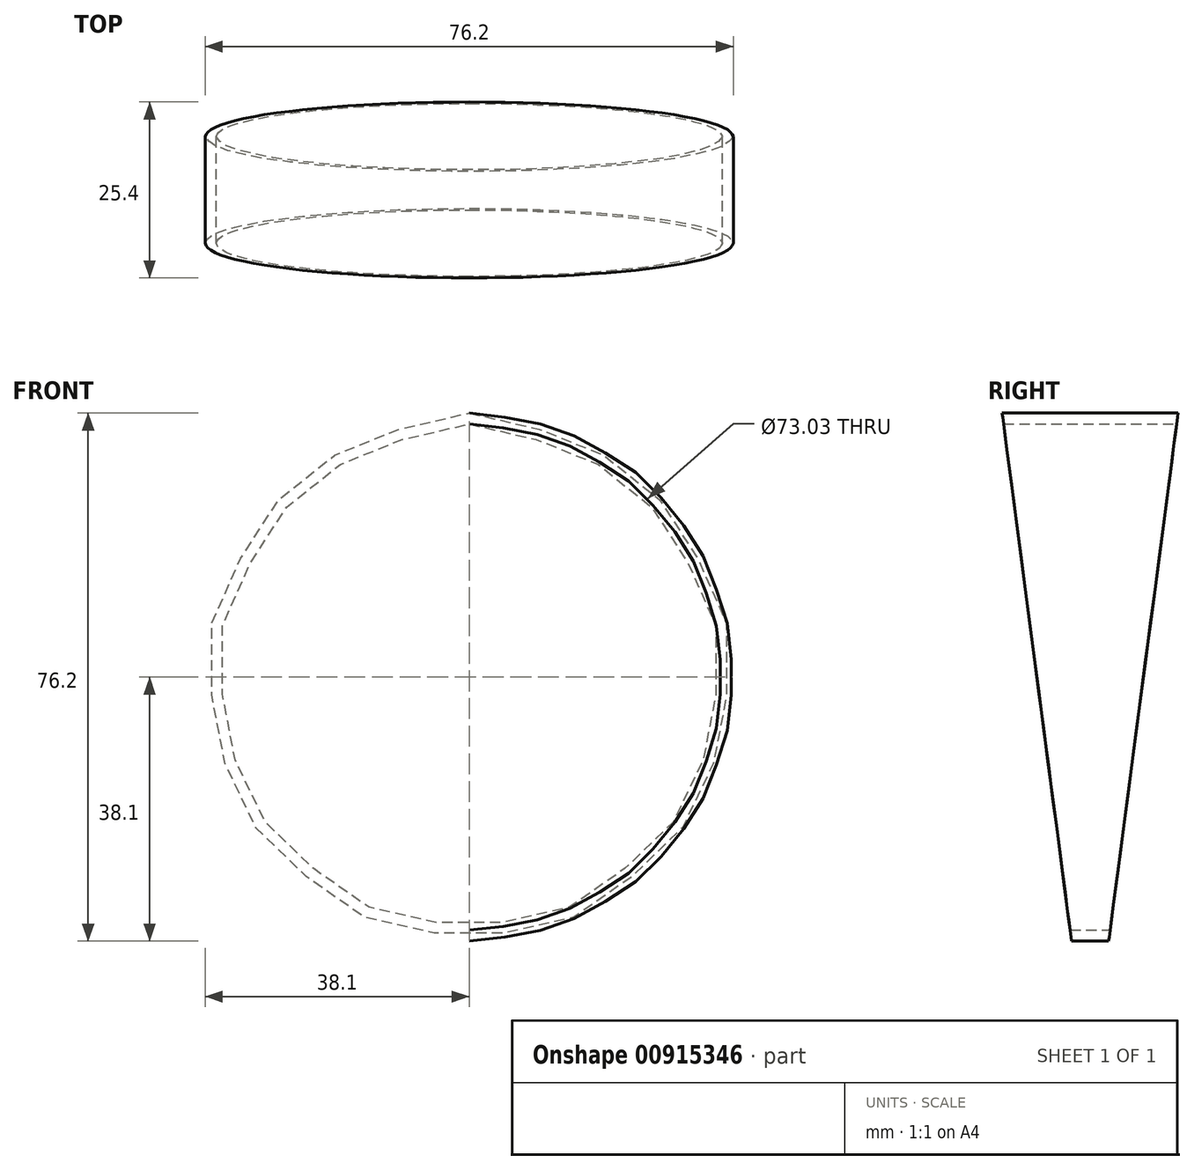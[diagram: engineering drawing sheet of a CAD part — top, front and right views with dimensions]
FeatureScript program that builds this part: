
annotation { "Feature Type Name" : "Feature", "Feature Type Description" : "" }
export const myFeature = defineFeature(function(context is Context, id is Id, definition is map)
    precondition{}
    {
        {
            var Q0;
            Q0=qCreatedBy(makeId("Front.planeOp"),FACE);
            var sketch = newSketch(context, id + "F0", { "sketchPlane" : qUnion([Q0])});
            skCircle(sketch, "E0", {"center": v(0, 38.1) * mm, "radius": 38.1 * mm});
            skCircle(sketch, "E1", {"center": v(0, 38.1) * mm, "radius": 36.51 * mm});
            skPoint(sketch, "E2", {"position": v(0, 0) * mm});
            skSolve(sketch);
        }
        {
            var Q0;
            Q0 = qSketchRegion(id + "F0", true);
            extrude(context, id + "F1", {"entities" : qUnion([Q0]), "endBound" : BoundingType.SYMMETRIC, "depth" : 25.4 * mm, "offsetDistance" : 25.4 * mm});
        }
        {
            var Q0;
            Q0=qCreatedBy(makeId("Right.planeOp"),FACE);
            var sketch = newSketch(context, id + "F2", { "sketchPlane" : qUnion([Q0])});
            skLineSegment(sketch, "E3", {"start": v(-2.67, 0) * mm, "end": v(-12.7, 76.2) * mm});
            skLineSegment(sketch, "E4", {"start": v(12.7, 76.2) * mm, "end": v(2.67, 0) * mm});
            skLineSegment(sketch, "E5", {"start": v(2.67, 0) * mm, "end": v(-2.67, 0) * mm});
            skPoint(sketch, "E6", {"position": v(0, 0) * mm});
            skLineSegment(sketch, "E7", {"start": v(12.7, 76.2) * mm, "end": v(12.7, -10.62) * mm});
            skLineSegment(sketch, "E8", {"start": v(-12.7, 76.2) * mm, "end": v(-12.7, -10.62) * mm});
            skLineSegment(sketch, "E9", {"start": v(-12.7, -10.62) * mm, "end": v(12.7, -10.62) * mm});
            skPoint(sketch, "E10", {"position": v(0, -10.62) * mm});
            skSolve(sketch);
        }
        {
            var Q0;
            Q0 = qSketchRegion(id + "F2", true);
            extrude(context, id + "F3", {"entities" : qUnion([Q0]), "operationType" : NewBodyOperationType.REMOVE, "endBound" : BoundingType.SYMMETRIC, "depth" : 76.2 * mm, "offsetDistance" : 25.4 * mm});
        }
    });
